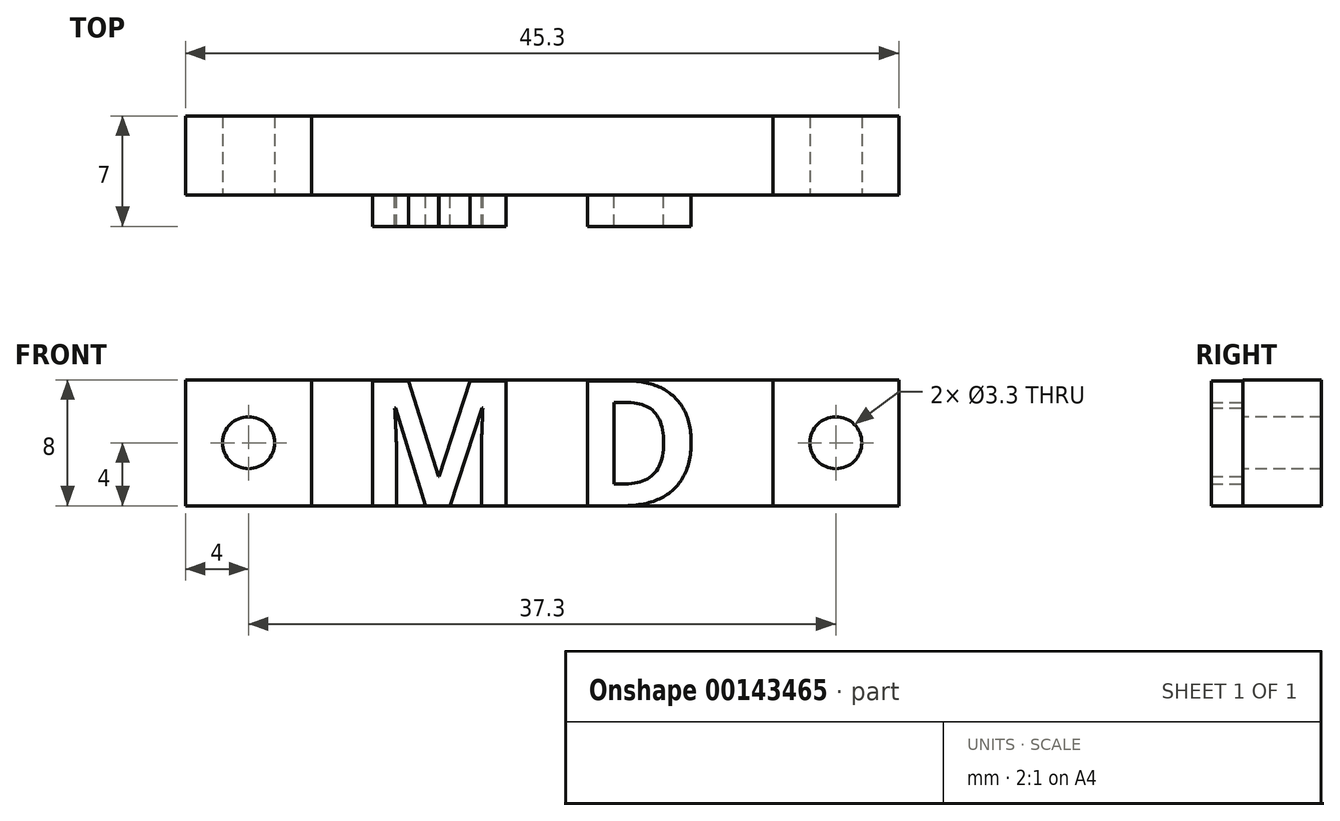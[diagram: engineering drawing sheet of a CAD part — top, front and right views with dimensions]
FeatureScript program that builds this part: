
annotation { "Feature Type Name" : "Feature", "Feature Type Description" : "" }
export const myFeature = defineFeature(function(context is Context, id is Id, definition is map)
    precondition{}
    {
        {
            var Q0;
            Q0=qCreatedBy(makeId("Front.planeOp"),FACE);
            var sketch = newSketch(context, id + "F0", { "sketchPlane" : qUnion([Q0])});
            skLineSegment(sketch, "E0.bottom", {"start": v(-22.65, -4) * mm, "end": v(-14.65, -4) * mm});
            skLineSegment(sketch, "E0.top", {"start": v(-22.65, 4) * mm, "end": v(-14.65, 4) * mm});
            skLineSegment(sketch, "E0.left", {"start": v(-22.65, -4) * mm, "end": v(-22.65, 4) * mm});
            skLineSegment(sketch, "E0.right", {"start": v(-14.65, -4) * mm, "end": v(-14.65, 4) * mm});
            skLineSegment(sketch, "E1.bottom", {"start": v(14.65, 4) * mm, "end": v(22.65, 4) * mm});
            skLineSegment(sketch, "E1.top", {"start": v(14.65, -4) * mm, "end": v(22.65, -4) * mm});
            skLineSegment(sketch, "E1.left", {"start": v(14.65, 4) * mm, "end": v(14.65, -4) * mm});
            skLineSegment(sketch, "E1.right", {"start": v(22.65, 4) * mm, "end": v(22.65, -4) * mm});
            skSolve(sketch);
        }
        {
            var Q0;
            Q0=makeQuery(id+"F0.imprint","IMPRINT",FACE,{"disambiguationData":[TD([[makeQuery(id+"F0.imprint","IMPRINT",EDGE,{"derivedFrom":sQuery(id+"F0.wireOp",EDGE,"E0.bottom")}),1.0]])]});
            var Q1;
            Q1=makeQuery(id+"F0.imprint","IMPRINT",FACE,{"disambiguationData":[TD([[makeQuery(id+"F0.imprint","IMPRINT",EDGE,{"derivedFrom":sQuery(id+"F0.wireOp",EDGE,"E1.bottom")}),-1.0]])]});
            extrude(context, id + "F1", {"entities" : qUnion([Q0, Q1]), "depth" : 5 * mm});
        }
        {
            var Q0;
            Q0=makeQuery(id+"F1.opExtrude","CAP_FACE",FACE,{"disambiguationData":[OSD([sQuery(id+"F0.wireOp",EDGE,"E0.bottom"),sQuery(id+"F0.wireOp",EDGE,"E0.top"),sQuery(id+"F0.wireOp",EDGE,"E0.left"),sQuery(id+"F0.wireOp",EDGE,"E0.right")])],"isStart":false});
            var sketch = newSketch(context, id + "F2", { "sketchPlane" : qUnion([Q0])});
            skLineSegment(sketch, "E2.0.0", {"start": v(-22.65, 4) * mm, "end": v(-22.65, -4) * mm});
            skLineSegment(sketch, "E2.0.1", {"start": v(-22.65, -4) * mm, "end": v(-14.65, -4) * mm});
            skLineSegment(sketch, "E2.0.2", {"start": v(-14.65, -4) * mm, "end": v(-14.65, 4) * mm});
            skLineSegment(sketch, "E2.0.3", {"start": v(-14.65, 4) * mm, "end": v(-22.65, 4) * mm});
            skLineSegment(sketch, "E3.0.0", {"start": v(22.65, 4) * mm, "end": v(14.65, 4) * mm});
            skLineSegment(sketch, "E3.0.1", {"start": v(14.65, 4) * mm, "end": v(14.65, -4) * mm});
            skLineSegment(sketch, "E3.0.2", {"start": v(14.65, -4) * mm, "end": v(22.65, -4) * mm});
            skLineSegment(sketch, "E3.0.3", {"start": v(22.65, -4) * mm, "end": v(22.65, 4) * mm});
            skPoint(sketch, "E4", {"position": v(-18.65, 0) * mm});
            skPoint(sketch, "E4.positionSnap0", {"position": v(-14.65, 0) * mm});
            skPoint(sketch, "E5", {"position": v(18.65, 0) * mm});
            skPoint(sketch, "E5.positionSnap0", {"position": v(22.65, 0) * mm});
            skSolve(sketch);
        }
        {
            var Q0;
            Q0=sQuery(id+"F2.wireOp",VERTEX,"E4");
            var Q1;
            Q1=sQuery(id+"F2.wireOp",VERTEX,"E5");
            var Q2;
            Q2=makeQuery(id+"F1.opExtrude","SWEPT_BODY",BODY,{"disambiguationData":[OSD([sQuery(id+"F0.wireOp",EDGE,"E0.bottom"),sQuery(id+"F0.wireOp",EDGE,"E0.top"),sQuery(id+"F0.wireOp",EDGE,"E0.left"),sQuery(id+"F0.wireOp",EDGE,"E0.right")])]});
            var Q3;
            Q3=makeQuery(id+"F1.opExtrude","SWEPT_BODY",BODY,{"disambiguationData":[OSD([sQuery(id+"F0.wireOp",EDGE,"E1.bottom"),sQuery(id+"F0.wireOp",EDGE,"E1.top"),sQuery(id+"F0.wireOp",EDGE,"E1.left"),sQuery(id+"F0.wireOp",EDGE,"E1.right")])]});
            hole(context, id + "F3", {"style" : HoleStyle.SIMPLE, "endStyle" : HoleEndStyle.BLIND, "holeDiameter" : 3.3 * mm, "holeDepth" : 25 * mm, "locations" : qUnion([Q0, Q1]), "scope" : qUnion([Q2, Q3])});
        }
        {
            var Q0;
            Q0=makeQuery(id+"F1.opExtrude","CAP_FACE",FACE,{"disambiguationData":[OSD([sQuery(id+"F0.wireOp",EDGE,"E0.bottom"),sQuery(id+"F0.wireOp",EDGE,"E0.top"),sQuery(id+"F0.wireOp",EDGE,"E0.left"),sQuery(id+"F0.wireOp",EDGE,"E0.right")])],"isStart":false});
            var sketch = newSketch(context, id + "F4", { "sketchPlane" : qUnion([Q0])});
            skLineSegment(sketch, "E6.0.0", {"start": v(-22.65, 4) * mm, "end": v(-22.65, -4) * mm});
            skLineSegment(sketch, "E6.0.1", {"start": v(-22.65, -4) * mm, "end": v(-14.65, -4) * mm});
            skLineSegment(sketch, "E6.0.2", {"start": v(-14.65, -4) * mm, "end": v(-14.65, 4) * mm});
            skLineSegment(sketch, "E6.0.3", {"start": v(-14.65, 4) * mm, "end": v(-22.65, 4) * mm});
            skLineSegment(sketch, "E7.0.0", {"start": v(22.65, 4) * mm, "end": v(14.65, 4) * mm});
            skLineSegment(sketch, "E7.0.1", {"start": v(14.65, 4) * mm, "end": v(14.65, -4) * mm});
            skLineSegment(sketch, "E7.0.2", {"start": v(14.65, -4) * mm, "end": v(22.65, -4) * mm});
            skLineSegment(sketch, "E7.0.3", {"start": v(22.65, -4) * mm, "end": v(22.65, 4) * mm});
            skLineSegment(sketch, "E8.bottom", {"start": v(-14.65, 4) * mm, "end": v(14.65, 4) * mm});
            skLineSegment(sketch, "E8.top", {"start": v(-14.65, -4) * mm, "end": v(14.65, -4) * mm});
            skLineSegment(sketch, "E8.left", {"start": v(-14.65, 4) * mm, "end": v(-14.65, -4) * mm});
            skSolve(sketch);
        }
        {
            var Q0;
            Q0=makeQuery(id+"F4.imprint","IMPRINT",FACE,{"disambiguationData":[TD([[makeQuery(id+"F4.imprint","IMPRINT",EDGE,{"derivedFrom":sQuery(id+"F4.wireOp",EDGE,"E8.bottom")}),-1.0]])]});
            extrude(context, id + "F5", {"entities" : qUnion([Q0]), "oppositeDirection" : true, "depth" : 5 * mm});
        }
        {
            var Q0;
            Q0=makeQuery(id+"F5.opExtrude","CAP_FACE",FACE,{"disambiguationData":[OSD([sQuery(id+"F4.wireOp",EDGE,"E8.bottom"),sQuery(id+"F4.wireOp",EDGE,"E8.top"),sQuery(id+"F4.wireOp",EDGE,"E8.left"),sQuery(id+"F4.wireOp",EDGE,"E7.0.1")])],"isStart":true});
            var sketch = newSketch(context, id + "F6", { "sketchPlane" : qUnion([Q0])});
            skText(sketch, "E9", { "text": " M.D. ", "fontName": "OpenSans-Bold.ttf"});
            const initialGuessF6  = {"E9": [-0.01465, -0.004, 1, 0, 0.008]};
            skSetInitialGuess(sketch, initialGuessF6);
            skSolve(sketch);
        }
        {
            var Q0;
            Q0=makeQuery(id+"F6.imprint","IMPRINT",FACE,{"disambiguationData":[TD([[makeQuery(id+"F6.imprint","IMPRINT",EDGE,{"derivedFrom":sQuery(id+"F6.wireOp",EDGE,"E9.sketch_text.stroke-0")}),-1.0]])]});
            var Q1;
            Q1=makeQuery(id+"F6.imprint","IMPRINT",FACE,{"disambiguationData":[TD([[makeQuery(id+"F6.imprint","IMPRINT",EDGE,{"derivedFrom":sQuery(id+"F6.wireOp",EDGE,"E9.sketch_text.stroke-27")}),-1.0]])]});
            extrude(context, id + "F7", {"entities" : qUnion([Q0, Q1]), "operationType" : NewBodyOperationType.ADD, "depth" : 2 * mm});
        }
    });
